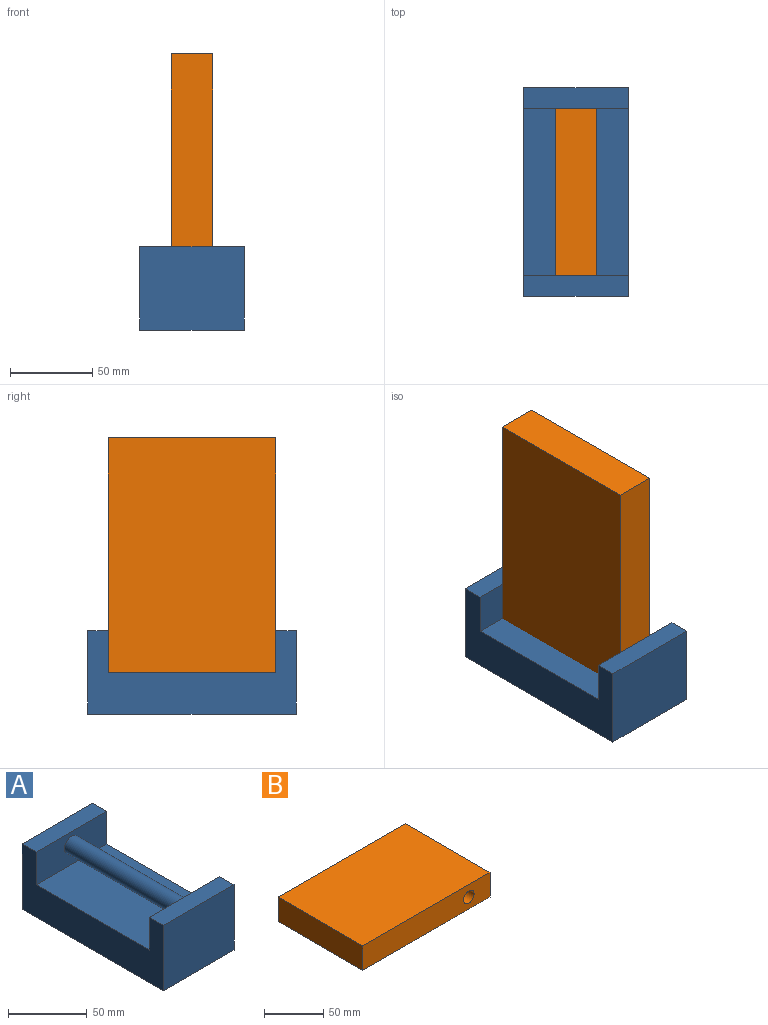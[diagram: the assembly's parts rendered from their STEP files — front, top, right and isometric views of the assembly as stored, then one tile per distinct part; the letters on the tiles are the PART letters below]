
ASSEMBLY  parts=2 mates=1
PART A: 11 faces, bbox 63.5x127x50.8 mm
  f0: plane 101.6x63.5mm, normal (0,0,1), area 6451.6mm2, adj f1,f3,f6,f8
  f1: plane 127x50.8mm, normal (1,0,0), area 3871mm2, adj f0,f2,f4,f5,f6,f7,f8,f9
  f2: plane 63.5x50.8mm, normal (0,1,0), area 3225.8mm2, adj f1,f3,f5,f7
  f3: plane 127x50.8mm, normal (-1,0,0), area 3871mm2, adj f0,f2,f4,f5,f6,f7,f8,f9
  f4: plane 63.5x50.8mm, normal (0,-1,0), area 3225.8mm2, adj f1,f3,f5,f9
  f5: plane 127x63.5mm, normal (0,0,-1), area 8064.5mm2, adj f1,f2,f3,f4
  f6: plane 63.5x25.4mm, normal (0,-1,0), area 1486.2mm2, adj f0,f1,f3,f7,f10
  f7: plane 63.5x12.7mm, normal (0,0,1), area 806.5mm2, adj f1,f2,f3,f6
  f8: plane 63.5x25.4mm, normal (0,1,0), area 1486.2mm2, adj f0,f1,f3,f9,f10
  f9: plane 63.5x12.7mm, normal (0,0,1), area 806.5mm2, adj f1,f3,f4,f8
  f10: cylinder r=6.35mm len=101.6mm, axis (0,-1,0), area 4053.7mm2, adj f6,f8
PART B: 7 faces, bbox 152.4x101.6x25.4 mm
  f0: plane 101.6x25.4mm, normal (1,0,0), area 2580.6mm2, adj f1,f3,f4,f5
  f1: plane 152.4x25.4mm, normal (0,1,0), area 3744.3mm2, adj f0,f2,f4,f5,f6
  f2: plane 101.6x25.4mm, normal (-1,0,0), area 2580.6mm2, adj f1,f3,f4,f5
  f3: plane 152.4x25.4mm, normal (0,-1,0), area 3744.3mm2, adj f0,f2,f4,f5,f6
  f4: plane 152.4x101.6mm, normal (0,0,1), area 15483.8mm2, adj f0,f1,f2,f3
  f5: plane 152.4x101.6mm, normal (0,0,-1), area 15483.8mm2, adj f0,f1,f2,f3
  f6: cylinder r=6.35mm len=101.6mm, axis (0,-1,0), area 4053.7mm2, adj f1,f3
PLACE A t=(23.07,2.86,-32.5)mm fixed
PLACE B rot(axis=(0,1,0),90deg) t=(10.37,2.86,59.3)mm
MATE revolute B.f6 <-> A.f10  axis (0,-1,0) through (23.07,-47.94,8.5)mm
